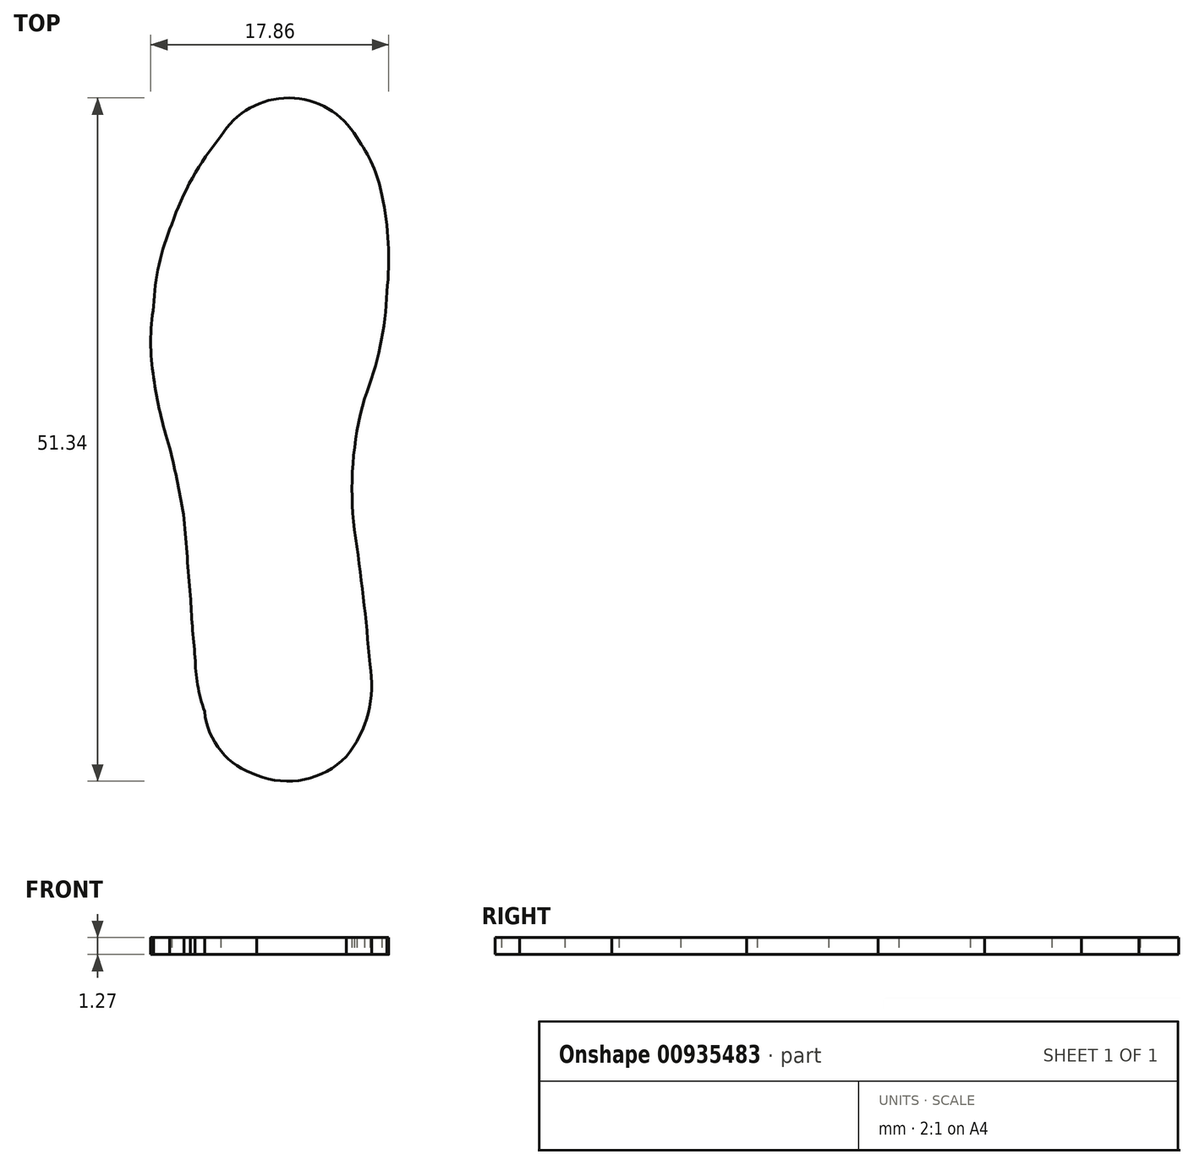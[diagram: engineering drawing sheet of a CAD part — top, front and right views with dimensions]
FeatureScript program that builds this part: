
annotation { "Feature Type Name" : "Feature", "Feature Type Description" : "" }
export const myFeature = defineFeature(function(context is Context, id is Id, definition is map)
    precondition{}
    {
        {
            var Q0;
            Q0=qCreatedBy(makeId("Top.planeOp"),FACE);
            var sketch = newSketch(context, id + "F0", { "sketchPlane" : qUnion([Q0])});
            skArc(sketch, "E0", {"start": v(-4.77, 21.55) * mm, "mid": v(-9.85, 24.53) * mm, "end": v(-14.98, 21.64) * mm});
            skArc(sketch, "E1", {"start": v(-14.98, 21.64) * mm, "mid": v(-17.13, 18.5) * mm, "end": v(-18.66, 15.02) * mm});
            skArc(sketch, "E2", {"start": v(-18.66, 15.02) * mm, "mid": v(-19.63, 12.01) * mm, "end": v(-20.03, 8.87) * mm});
            skArc(sketch, "E3", {"start": v(-20.03, 8.87) * mm, "mid": v(-20.24, 6.2) * mm, "end": v(-20.03, 3.5) * mm});
            skArc(sketch, "E4", {"start": v(-20.03, 3.5) * mm, "mid": v(-19.54, 0.85) * mm, "end": v(-18.82, -1.76) * mm});
            skArc(sketch, "E5", {"start": v(-17.73, -7.11) * mm, "mid": v(-18.22, -4.42) * mm, "end": v(-18.82, -1.76) * mm});
            skArc(sketch, "E6", {"start": v(-17.73, -7.11) * mm, "mid": v(-17.5, -9.99) * mm, "end": v(-17.26, -12.86) * mm});
            skArc(sketch, "E7", {"start": v(-17.26, -12.86) * mm, "mid": v(-17.12, -15.19) * mm, "end": v(-16.9, -17.5) * mm});
            skArc(sketch, "E8", {"start": v(-16.9, -17.5) * mm, "mid": v(-16.72, -19.57) * mm, "end": v(-16.2, -21.58) * mm});
            skArc(sketch, "E9", {"start": v(-16.2, -21.58) * mm, "mid": v(-14.96, -24.55) * mm, "end": v(-12.28, -26.34) * mm});
            skArc(sketch, "E10", {"start": v(-12.28, -26.34) * mm, "mid": v(-8.7, -26.68) * mm, "end": v(-5.56, -24.96) * mm});
            skArc(sketch, "E11", {"start": v(-5.56, -24.96) * mm, "mid": v(-3.92, -21.7) * mm, "end": v(-3.8, -18.05) * mm});
            skArc(sketch, "E12", {"start": v(-3.8, -18.05) * mm, "mid": v(-4.28, -12.97) * mm, "end": v(-4.95, -7.92) * mm});
            skArc(sketch, "E13", {"start": v(-4.2, 1.94) * mm, "mid": v(-5.06, -2.95) * mm, "end": v(-4.95, -7.92) * mm});
            skArc(sketch, "E14", {"start": v(-4.2, 1.94) * mm, "mid": v(-3.01, 5.89) * mm, "end": v(-2.5, 9.97) * mm});
            skArc(sketch, "E15", {"start": v(-2.5, 9.97) * mm, "mid": v(-2.4, 13.61) * mm, "end": v(-2.88, 17.22) * mm});
            skArc(sketch, "E16", {"start": v(-2.88, 17.22) * mm, "mid": v(-3.6, 19.49) * mm, "end": v(-4.77, 21.55) * mm});
            skSolve(sketch);
        }
        {
            var Q0;
            Q0=qSketchRegion(id+"F0",true);
            extrude(context, id + "F1", {"entities" : qUnion([Q0]), "depth" : 1.27 * mm, "offsetDistance" : 25.4 * mm});
        }
    });
